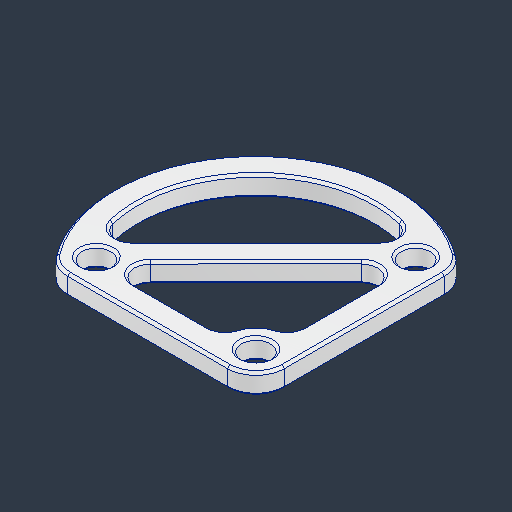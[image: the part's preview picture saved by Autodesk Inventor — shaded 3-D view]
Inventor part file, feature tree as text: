
AUTODESK INVENTOR PART (.ipt)
format: ipt  version: 2024.3 (Build 283343000, 343)  size: 169,472 bytes
history: native  units: in
note: dims shown in document units (in); Inventor stores cm internally (conversion verified against a paired STEP export)
features: chamfer x1
ambient origin geometry x8: Origin, YZ Plane, XZ Plane, XY Plane, X Axis, Y Axis, Z Axis, Center Point
bodies: Solid12 (feature_tree)
feature tree (1):
  chamfer  "Chamfer4"  [1 undecoded]
note: 1 required parameter value undecoded (feature->parameter linkage not recoverable at this tier; creation-order binding heuristic only, values carry confidence <= 0.55)
